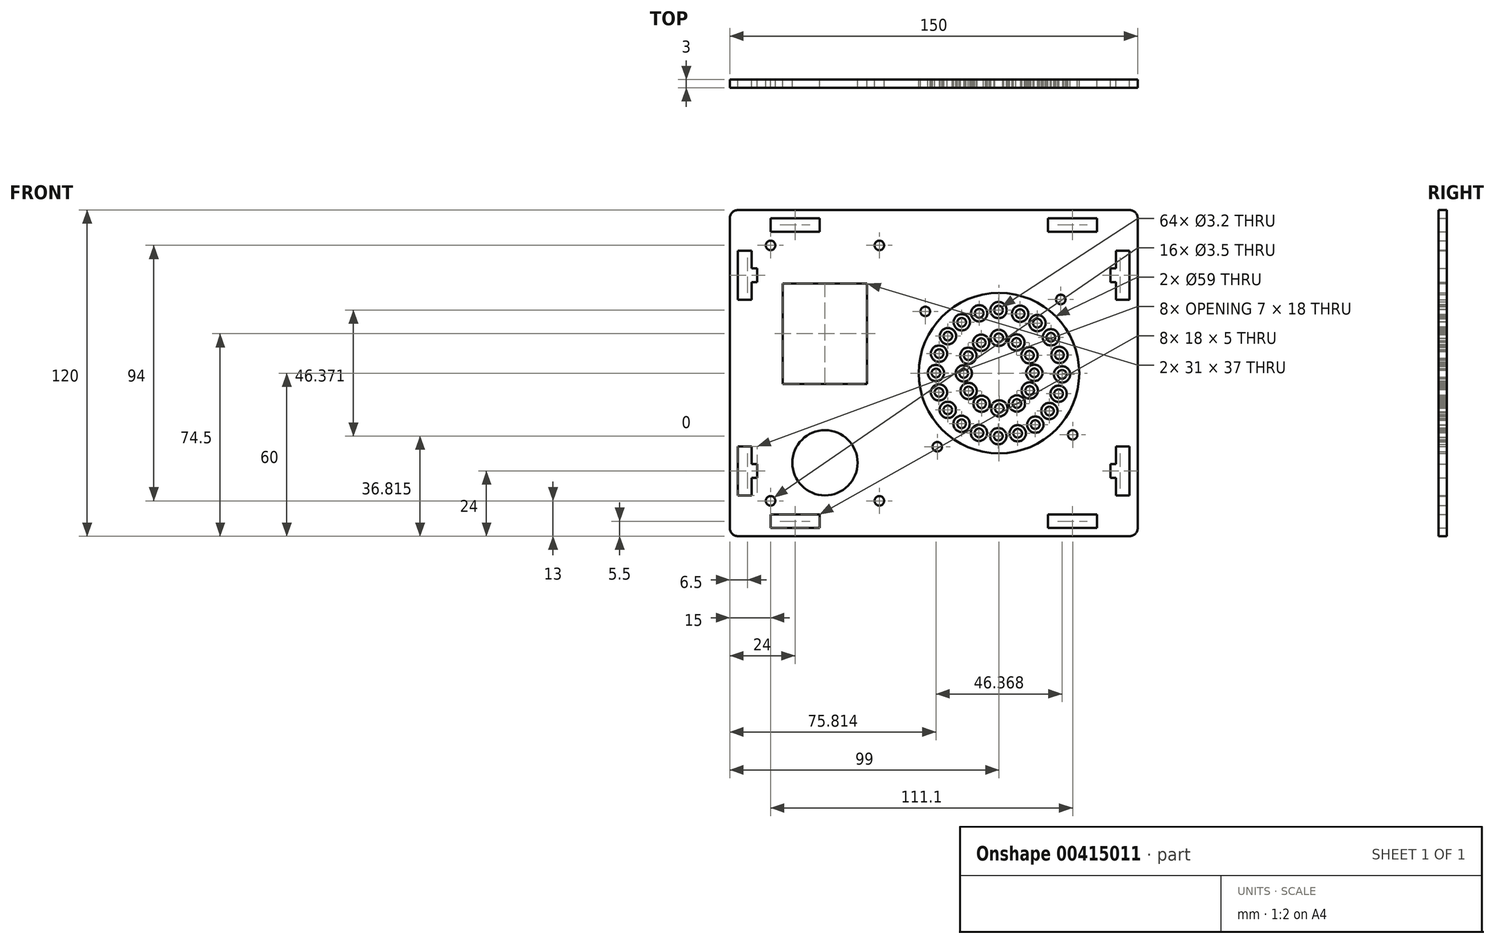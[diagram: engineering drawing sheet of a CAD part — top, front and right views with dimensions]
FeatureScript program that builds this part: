
annotation { "Feature Type Name" : "Feature", "Feature Type Description" : "" }
export const myFeature = defineFeature(function(context is Context, id is Id, definition is map)
    precondition{}
    {
        {
            var Q0;
            Q0=qCreatedBy(makeId("Front.planeOp"),FACE);
            var sketch = newSketch(context, id + "F0", { "sketchPlane" : qUnion([Q0])});
            skLineSegment(sketch, "E0.bottom", {"start": v(-72, 60) * mm, "end": v(72, 60) * mm});
            skLineSegment(sketch, "E0.top", {"start": v(-72, -60) * mm, "end": v(72, -60) * mm});
            skLineSegment(sketch, "E0.left", {"start": v(-75, 57) * mm, "end": v(-75, -57) * mm});
            skLineSegment(sketch, "E0.right", {"start": v(75, 57) * mm, "end": v(75, -57) * mm});
            skPoint(sketch, "E1.visualSharp", {"position": v(-75, 60) * mm});
            skArc(sketch, "E1.filletArc", {"start": v(-72, 60) * mm, "mid": v(-74.12, 59.12) * mm, "end": v(-75, 57) * mm});
            skPoint(sketch, "E2.visualSharp", {"position": v(75, 60) * mm});
            skArc(sketch, "E2.filletArc", {"start": v(75, 57) * mm, "mid": v(74.12, 59.12) * mm, "end": v(72, 60) * mm});
            skPoint(sketch, "E3.visualSharp", {"position": v(75, -60) * mm});
            skArc(sketch, "E3.filletArc", {"start": v(72, -60) * mm, "mid": v(74.12, -59.12) * mm, "end": v(75, -57) * mm});
            skPoint(sketch, "E4.visualSharp", {"position": v(-75, -60) * mm});
            skArc(sketch, "E4.filletArc", {"start": v(-75, -57) * mm, "mid": v(-74.12, -59.12) * mm, "end": v(-72, -60) * mm});
            skLineSegment(sketch, "E5.bottom", {"start": v(-60, 57) * mm, "end": v(-42, 57) * mm});
            skLineSegment(sketch, "E5.top", {"start": v(-60, 52) * mm, "end": v(-42, 52) * mm});
            skLineSegment(sketch, "E5.left", {"start": v(-60, 57) * mm, "end": v(-60, 52) * mm});
            skLineSegment(sketch, "E5.right", {"start": v(-42, 57) * mm, "end": v(-42, 52) * mm});
            skLineSegment(sketch, "E6.bottom", {"start": v(42, 57) * mm, "end": v(60, 57) * mm});
            skLineSegment(sketch, "E6.top", {"start": v(42, 52) * mm, "end": v(60, 52) * mm});
            skLineSegment(sketch, "E6.left", {"start": v(42, 57) * mm, "end": v(42, 52) * mm});
            skLineSegment(sketch, "E6.right", {"start": v(60, 57) * mm, "end": v(60, 52) * mm});
            skLineSegment(sketch, "E7.bottom", {"start": v(72, 45) * mm, "end": v(67, 45) * mm});
            skLineSegment(sketch, "E7.top", {"start": v(72, 27) * mm, "end": v(67, 27) * mm});
            skLineSegment(sketch, "E7.left", {"start": v(72, 45) * mm, "end": v(72, 27) * mm});
            skLineSegment(sketch, "E7.right", {"start": v(67, 45) * mm, "end": v(67, 38.5) * mm});
            skLineSegment(sketch, "E8.bottom", {"start": v(72, -27) * mm, "end": v(67, -27) * mm});
            skLineSegment(sketch, "E8.top", {"start": v(72, -45) * mm, "end": v(67, -45) * mm});
            skLineSegment(sketch, "E8.left", {"start": v(72, -27) * mm, "end": v(72, -45) * mm});
            skLineSegment(sketch, "E8.right", {"start": v(67, -27) * mm, "end": v(67, -33.5) * mm});
            skLineSegment(sketch, "E9.bottom", {"start": v(60, -57) * mm, "end": v(42, -57) * mm});
            skLineSegment(sketch, "E9.top", {"start": v(60, -52) * mm, "end": v(42, -52) * mm});
            skLineSegment(sketch, "E9.left", {"start": v(60, -57) * mm, "end": v(60, -52) * mm});
            skLineSegment(sketch, "E9.right", {"start": v(42, -57) * mm, "end": v(42, -52) * mm});
            skLineSegment(sketch, "E10.bottom", {"start": v(-42, -57) * mm, "end": v(-60, -57) * mm});
            skLineSegment(sketch, "E10.top", {"start": v(-42, -52) * mm, "end": v(-60, -52) * mm});
            skLineSegment(sketch, "E10.left", {"start": v(-42, -57) * mm, "end": v(-42, -52) * mm});
            skLineSegment(sketch, "E10.right", {"start": v(-60, -57) * mm, "end": v(-60, -52) * mm});
            skLineSegment(sketch, "E11.bottom", {"start": v(-67, -27) * mm, "end": v(-72, -27) * mm});
            skLineSegment(sketch, "E11.top", {"start": v(-67, -45) * mm, "end": v(-72, -45) * mm});
            skLineSegment(sketch, "E11.left", {"start": v(-67, -33.5) * mm, "end": v(-67, -27) * mm});
            skLineSegment(sketch, "E11.right", {"start": v(-72, -45) * mm, "end": v(-72, -27) * mm});
            skLineSegment(sketch, "E12.bottom", {"start": v(-67, 27) * mm, "end": v(-72, 27) * mm});
            skLineSegment(sketch, "E12.top", {"start": v(-67, 45) * mm, "end": v(-72, 45) * mm});
            skLineSegment(sketch, "E12.left", {"start": v(-67, 27) * mm, "end": v(-67, 33.5) * mm});
            skLineSegment(sketch, "E12.right", {"start": v(-72, 27) * mm, "end": v(-72, 45) * mm});
            skCircle(sketch, "E13", {"center": v(24, 0) * mm, "radius": 29.5 * mm});
            skCircle(sketch, "E14", {"center": v(46.7, 27.1) * mm, "radius": 1.75 * mm});
            skCircle(sketch, "E15", {"center": v(-3.1, 22.7) * mm, "radius": 1.75 * mm});
            skCircle(sketch, "E16", {"center": v(1.3, -27.1) * mm, "radius": 1.75 * mm});
            skCircle(sketch, "E17", {"center": v(51.1, -22.7) * mm, "radius": 1.75 * mm});
            skLineSegment(sketch, "E18", {"start": v(-75, 0) * mm, "end": v(75, 0) * mm, "construction": true});
            skLineSegment(sketch, "E19.bottom", {"start": v(-17, 50) * mm, "end": v(-63, 50) * mm, "construction": true});
            skLineSegment(sketch, "E19.top", {"start": v(-17, -50) * mm, "end": v(-63, -50) * mm, "construction": true});
            skLineSegment(sketch, "E19.left", {"start": v(-17, 50) * mm, "end": v(-17, -50) * mm, "construction": true});
            skLineSegment(sketch, "E19.right", {"start": v(-63, 50) * mm, "end": v(-63, -50) * mm, "construction": true});
            skPoint(sketch, "E19.middle", {"position": v(-40, 0) * mm});
            skLineSegment(sketch, "E20", {"start": v(-40, 0) * mm, "end": v(-40, 15.63) * mm, "construction": true});
            skCircle(sketch, "E21", {"center": v(-60, 47) * mm, "radius": 1.75 * mm});
            skCircle(sketch, "E22.MirrorC", {"center": v(-20, 47) * mm, "radius": 1.75 * mm});
            skCircle(sketch, "E23.MirrorC", {"center": v(-20, -47) * mm, "radius": 1.75 * mm});
            skCircle(sketch, "E24.MirrorC", {"center": v(-60, -47) * mm, "radius": 1.75 * mm});
            skLineSegment(sketch, "E25.bottom", {"start": v(-24.5, -4) * mm, "end": v(-55.5, -4) * mm});
            skLineSegment(sketch, "E25.top", {"start": v(-24.5, 33) * mm, "end": v(-55.5, 33) * mm});
            skLineSegment(sketch, "E25.left", {"start": v(-24.5, -4) * mm, "end": v(-24.5, 33) * mm});
            skLineSegment(sketch, "E25.right", {"start": v(-55.5, -4) * mm, "end": v(-55.5, 33) * mm});
            skPoint(sketch, "E25.middle", {"position": v(-40, 14.5) * mm});
            skCircle(sketch, "E26", {"center": v(-40, -33) * mm, "radius": 12 * mm});
            skLineSegment(sketch, "E27.bottom", {"start": v(62, -43) * mm, "end": v(-14, -43) * mm, "construction": true});
            skLineSegment(sketch, "E27.top", {"start": v(62, 43) * mm, "end": v(-14, 43) * mm, "construction": true});
            skLineSegment(sketch, "E27.left", {"start": v(62, -43) * mm, "end": v(62, 43) * mm, "construction": true});
            skLineSegment(sketch, "E27.right", {"start": v(-14, -43) * mm, "end": v(-14, 43) * mm, "construction": true});
            skLineSegment(sketch, "E28", {"start": v(-67, 38.5) * mm, "end": v(-65, 38.5) * mm});
            skLineSegment(sketch, "E29", {"start": v(-65, 38.5) * mm, "end": v(-65, 33.5) * mm});
            skLineSegment(sketch, "E30", {"start": v(-65, 33.5) * mm, "end": v(-67, 33.5) * mm});
            skLineSegment(sketch, "E31.trimOffspring", {"start": v(-67, 38.5) * mm, "end": v(-67, 45) * mm});
            skLineSegment(sketch, "E32", {"start": v(-72, 36) * mm, "end": v(-68.51, 36) * mm, "construction": true});
            skPoint(sketch, "E32.endSnap0", {"position": v(-72, 36) * mm});
            skLineSegment(sketch, "E33.MirrorCS", {"start": v(65, 38.5) * mm, "end": v(65, 33.5) * mm});
            skLineSegment(sketch, "E34.MirrorCS", {"start": v(67, 38.5) * mm, "end": v(65, 38.5) * mm});
            skLineSegment(sketch, "E35.MirrorCS", {"start": v(65, 33.5) * mm, "end": v(67, 33.5) * mm});
            skLineSegment(sketch, "E36.MirrorCS", {"start": v(-67, -38.5) * mm, "end": v(-65, -38.5) * mm});
            skLineSegment(sketch, "E37.MirrorCS", {"start": v(-65, -38.5) * mm, "end": v(-65, -33.5) * mm});
            skLineSegment(sketch, "E38.MirrorCS", {"start": v(-65, -33.5) * mm, "end": v(-67, -33.5) * mm});
            skLineSegment(sketch, "E39.MirrorCS", {"start": v(67, -38.5) * mm, "end": v(65, -38.5) * mm});
            skLineSegment(sketch, "E40.MirrorCS", {"start": v(65, -38.5) * mm, "end": v(65, -33.5) * mm});
            skLineSegment(sketch, "E41.MirrorCS", {"start": v(65, -33.5) * mm, "end": v(67, -33.5) * mm});
            skLineSegment(sketch, "E42.trimOffspring", {"start": v(67, 33.5) * mm, "end": v(67, 27) * mm});
            skLineSegment(sketch, "E43.trimOffspring", {"start": v(67, -38.5) * mm, "end": v(67, -45) * mm});
            skLineSegment(sketch, "E44.trimOffspring", {"start": v(-67, -45) * mm, "end": v(-67, -38.5) * mm});
            skSolve(sketch);
        }
        {
            var Q0;
            Q0=makeQuery(id+"F0.imprint","IMPRINT",FACE,{"disambiguationData":[TD([[makeQuery(id+"F0.imprint","IMPRINT",EDGE,{"derivedFrom":sQuery(id+"F0.wireOp",EDGE,"E0.bottom")}),-1.0]])]});
            extrude(context, id + "F1", {"entities" : qUnion([Q0]), "depth" : 3 * mm});
        }
        {
            var Q0;
            Q0=makeQuery(id+"F1.opExtrude","CAP_FACE",FACE,{"disambiguationData":[OSD([sQuery(id+"F0.wireOp",EDGE,"E0.bottom"),sQuery(id+"F0.wireOp",EDGE,"E0.top"),sQuery(id+"F0.wireOp",EDGE,"E0.left"),sQuery(id+"F0.wireOp",EDGE,"E0.right"),sQuery(id+"F0.wireOp",EDGE,"E1.filletArc"),sQuery(id+"F0.wireOp",EDGE,"E2.filletArc"),sQuery(id+"F0.wireOp",EDGE,"E3.filletArc"),sQuery(id+"F0.wireOp",EDGE,"E4.filletArc"),sQuery(id+"F0.wireOp",EDGE,"E5.bottom"),sQuery(id+"F0.wireOp",EDGE,"E5.top"),sQuery(id+"F0.wireOp",EDGE,"E5.left"),sQuery(id+"F0.wireOp",EDGE,"E5.right"),sQuery(id+"F0.wireOp",EDGE,"E6.bottom"),sQuery(id+"F0.wireOp",EDGE,"E6.top"),sQuery(id+"F0.wireOp",EDGE,"E6.left"),sQuery(id+"F0.wireOp",EDGE,"E6.right"),sQuery(id+"F0.wireOp",EDGE,"E7.bottom"),sQuery(id+"F0.wireOp",EDGE,"E7.top"),sQuery(id+"F0.wireOp",EDGE,"E7.left"),sQuery(id+"F0.wireOp",EDGE,"E7.right"),sQuery(id+"F0.wireOp",EDGE,"E8.bottom"),sQuery(id+"F0.wireOp",EDGE,"E8.top"),sQuery(id+"F0.wireOp",EDGE,"E8.left"),sQuery(id+"F0.wireOp",EDGE,"E8.right"),sQuery(id+"F0.wireOp",EDGE,"E9.bottom"),sQuery(id+"F0.wireOp",EDGE,"E9.top"),sQuery(id+"F0.wireOp",EDGE,"E9.left"),sQuery(id+"F0.wireOp",EDGE,"E9.right"),sQuery(id+"F0.wireOp",EDGE,"E10.bottom"),sQuery(id+"F0.wireOp",EDGE,"E10.top"),sQuery(id+"F0.wireOp",EDGE,"E10.left"),sQuery(id+"F0.wireOp",EDGE,"E10.right"),sQuery(id+"F0.wireOp",EDGE,"E11.bottom"),sQuery(id+"F0.wireOp",EDGE,"E11.top"),sQuery(id+"F0.wireOp",EDGE,"E11.left"),sQuery(id+"F0.wireOp",EDGE,"E11.right"),sQuery(id+"F0.wireOp",EDGE,"E12.bottom"),sQuery(id+"F0.wireOp",EDGE,"E12.top"),sQuery(id+"F0.wireOp",EDGE,"E12.left"),sQuery(id+"F0.wireOp",EDGE,"E12.right"),sQuery(id+"F0.wireOp",EDGE,"E13"),sQuery(id+"F0.wireOp",EDGE,"E14"),sQuery(id+"F0.wireOp",EDGE,"E15"),sQuery(id+"F0.wireOp",EDGE,"E16"),sQuery(id+"F0.wireOp",EDGE,"E17"),sQuery(id+"F0.wireOp",EDGE,"E21"),sQuery(id+"F0.wireOp",EDGE,"E22.MirrorC"),sQuery(id+"F0.wireOp",EDGE,"E23.MirrorC"),sQuery(id+"F0.wireOp",EDGE,"E24.MirrorC"),sQuery(id+"F0.wireOp",EDGE,"E25.bottom"),sQuery(id+"F0.wireOp",EDGE,"E25.top"),sQuery(id+"F0.wireOp",EDGE,"E25.left"),sQuery(id+"F0.wireOp",EDGE,"E25.right"),sQuery(id+"F0.wireOp",EDGE,"E26"),sQuery(id+"F0.wireOp",EDGE,"E28"),sQuery(id+"F0.wireOp",EDGE,"E29"),sQuery(id+"F0.wireOp",EDGE,"E30"),sQuery(id+"F0.wireOp",EDGE,"E31.trimOffspring"),sQuery(id+"F0.wireOp",EDGE,"E33.MirrorCS"),sQuery(id+"F0.wireOp",EDGE,"E34.MirrorCS"),sQuery(id+"F0.wireOp",EDGE,"E35.MirrorCS"),sQuery(id+"F0.wireOp",EDGE,"E36.MirrorCS"),sQuery(id+"F0.wireOp",EDGE,"E37.MirrorCS"),sQuery(id+"F0.wireOp",EDGE,"E38.MirrorCS"),sQuery(id+"F0.wireOp",EDGE,"E39.MirrorCS"),sQuery(id+"F0.wireOp",EDGE,"E40.MirrorCS"),sQuery(id+"F0.wireOp",EDGE,"E41.MirrorCS"),sQuery(id+"F0.wireOp",EDGE,"E42.trimOffspring"),sQuery(id+"F0.wireOp",EDGE,"E43.trimOffspring"),sQuery(id+"F0.wireOp",EDGE,"E44.trimOffspring")])],"isStart":true});
            var sketch = newSketch(context, id + "F2", { "sketchPlane" : qUnion([Q0])});
            skCircle(sketch, "E45", {"center": v(-23.83, 23.19) * mm, "radius": 3 * mm});
            skCircle(sketch, "E46", {"center": v(-23.83, 23.19) * mm, "radius": 1.6 * mm});
            skCircle(sketch, "E47.1.0", {"center": v(-16.71, 22.01) * mm, "radius": 1.6 * mm});
            skCircle(sketch, "E47.1.1", {"center": v(-16.71, 22.01) * mm, "radius": 3 * mm});
            skCircle(sketch, "E47.2.0", {"center": v(-10.3, 18.7) * mm, "radius": 1.6 * mm});
            skCircle(sketch, "E47.2.1", {"center": v(-10.3, 18.7) * mm, "radius": 3 * mm});
            skCircle(sketch, "E47.3.0", {"center": v(-5.22, 13.6) * mm, "radius": 1.6 * mm});
            skCircle(sketch, "E47.3.1", {"center": v(-5.22, 13.6) * mm, "radius": 3 * mm});
            skCircle(sketch, "E47.4.0", {"center": v(-1.95, 7.17) * mm, "radius": 1.6 * mm});
            skCircle(sketch, "E47.4.1", {"center": v(-1.95, 7.17) * mm, "radius": 3 * mm});
            skCircle(sketch, "E47.5.0", {"center": v(-0.81, 0.04) * mm, "radius": 1.6 * mm});
            skCircle(sketch, "E47.5.1", {"center": v(-0.81, 0.04) * mm, "radius": 3 * mm});
            skCircle(sketch, "E47.6.0", {"center": v(-1.92, -7.08) * mm, "radius": 1.6 * mm});
            skCircle(sketch, "E47.6.1", {"center": v(-1.92, -7.08) * mm, "radius": 3 * mm});
            skCircle(sketch, "E47.7.0", {"center": v(-5.17, -13.52) * mm, "radius": 1.6 * mm});
            skCircle(sketch, "E47.7.1", {"center": v(-5.17, -13.52) * mm, "radius": 3 * mm});
            skCircle(sketch, "E47.8.0", {"center": v(-10.23, -18.66) * mm, "radius": 1.6 * mm});
            skCircle(sketch, "E47.8.1", {"center": v(-10.23, -18.66) * mm, "radius": 3 * mm});
            skCircle(sketch, "E47.9.0", {"center": v(-16.63, -21.98) * mm, "radius": 1.6 * mm});
            skCircle(sketch, "E47.9.1", {"center": v(-16.63, -21.98) * mm, "radius": 3 * mm});
            skCircle(sketch, "E47.10.0", {"center": v(-23.74, -23.19) * mm, "radius": 1.6 * mm});
            skCircle(sketch, "E47.10.1", {"center": v(-23.74, -23.19) * mm, "radius": 3 * mm});
            skCircle(sketch, "E47.11.0", {"center": v(-30.88, -22.14) * mm, "radius": 1.6 * mm});
            skCircle(sketch, "E47.11.1", {"center": v(-30.88, -22.14) * mm, "radius": 3 * mm});
            skCircle(sketch, "E47.12.0", {"center": v(-37.35, -18.96) * mm, "radius": 1.6 * mm});
            skCircle(sketch, "E47.12.1", {"center": v(-37.35, -18.96) * mm, "radius": 3 * mm});
            skCircle(sketch, "E47.13.0", {"center": v(-42.53, -13.94) * mm, "radius": 1.6 * mm});
            skCircle(sketch, "E47.13.1", {"center": v(-42.53, -13.94) * mm, "radius": 3 * mm});
            skCircle(sketch, "E47.14.0", {"center": v(-45.92, -7.57) * mm, "radius": 1.6 * mm});
            skCircle(sketch, "E47.14.1", {"center": v(-45.92, -7.57) * mm, "radius": 3 * mm});
            skCircle(sketch, "E47.15.0", {"center": v(-47.18, -0.47) * mm, "radius": 1.6 * mm});
            skCircle(sketch, "E47.15.1", {"center": v(-47.18, -0.47) * mm, "radius": 3 * mm});
            skCircle(sketch, "E47.16.0", {"center": v(-46.2, 6.68) * mm, "radius": 1.6 * mm});
            skCircle(sketch, "E47.16.1", {"center": v(-46.2, 6.68) * mm, "radius": 3 * mm});
            skCircle(sketch, "E47.17.0", {"center": v(-43.08, 13.18) * mm, "radius": 1.6 * mm});
            skCircle(sketch, "E47.17.1", {"center": v(-43.08, 13.18) * mm, "radius": 3 * mm});
            skCircle(sketch, "E47.18.0", {"center": v(-38.1, 18.4) * mm, "radius": 1.6 * mm});
            skCircle(sketch, "E47.18.1", {"center": v(-38.1, 18.4) * mm, "radius": 3 * mm});
            skCircle(sketch, "E47.19.0", {"center": v(-31.77, 21.85) * mm, "radius": 1.6 * mm});
            skCircle(sketch, "E47.19.1", {"center": v(-31.77, 21.85) * mm, "radius": 3 * mm});
            skPoint(sketch, "E47.center", {"position": v(-24, 0) * mm});
            skLineSegment(sketch, "E47.anchor1", {"start": v(-24, 0) * mm, "end": v(-23.83, 23.19) * mm, "construction": true});
            skLineSegment(sketch, "E47.anchor2", {"start": v(-24, 0) * mm, "end": v(-31.77, 21.85) * mm, "construction": true});
            skCircle(sketch, "E48", {"center": v(-23.9, 12.97) * mm, "radius": 3 * mm});
            skCircle(sketch, "E49", {"center": v(-23.9, 12.97) * mm, "radius": 1.6 * mm});
            skCircle(sketch, "E50.1.0", {"center": v(-17.43, 11.19) * mm, "radius": 3 * mm});
            skCircle(sketch, "E50.1.1", {"center": v(-17.43, 11.19) * mm, "radius": 1.6 * mm});
            skCircle(sketch, "E50.2.0", {"center": v(-12.72, 6.4) * mm, "radius": 3 * mm});
            skCircle(sketch, "E50.2.1", {"center": v(-12.72, 6.4) * mm, "radius": 1.6 * mm});
            skCircle(sketch, "E50.3.0", {"center": v(-11.03, -0.1) * mm, "radius": 3 * mm});
            skCircle(sketch, "E50.3.1", {"center": v(-11.03, -0.1) * mm, "radius": 1.6 * mm});
            skCircle(sketch, "E50.4.0", {"center": v(-12.81, -6.57) * mm, "radius": 3 * mm});
            skCircle(sketch, "E50.4.1", {"center": v(-12.81, -6.57) * mm, "radius": 1.6 * mm});
            skCircle(sketch, "E50.5.0", {"center": v(-17.6, -11.28) * mm, "radius": 3 * mm});
            skCircle(sketch, "E50.5.1", {"center": v(-17.6, -11.28) * mm, "radius": 1.6 * mm});
            skCircle(sketch, "E50.6.0", {"center": v(-24.1, -12.97) * mm, "radius": 3 * mm});
            skCircle(sketch, "E50.6.1", {"center": v(-24.1, -12.97) * mm, "radius": 1.6 * mm});
            skCircle(sketch, "E50.7.0", {"center": v(-30.57, -11.19) * mm, "radius": 3 * mm});
            skCircle(sketch, "E50.7.1", {"center": v(-30.57, -11.19) * mm, "radius": 1.6 * mm});
            skCircle(sketch, "E50.8.0", {"center": v(-35.28, -6.4) * mm, "radius": 3 * mm});
            skCircle(sketch, "E50.8.1", {"center": v(-35.28, -6.4) * mm, "radius": 1.6 * mm});
            skCircle(sketch, "E50.9.0", {"center": v(-36.97, 0.1) * mm, "radius": 3 * mm});
            skCircle(sketch, "E50.9.1", {"center": v(-36.97, 0.1) * mm, "radius": 1.6 * mm});
            skCircle(sketch, "E50.10.0", {"center": v(-35.19, 6.57) * mm, "radius": 3 * mm});
            skCircle(sketch, "E50.10.1", {"center": v(-35.19, 6.57) * mm, "radius": 1.6 * mm});
            skCircle(sketch, "E50.11.0", {"center": v(-30.4, 11.28) * mm, "radius": 3 * mm});
            skCircle(sketch, "E50.11.1", {"center": v(-30.4, 11.28) * mm, "radius": 1.6 * mm});
            skLineSegment(sketch, "E50.anchor1", {"start": v(-24, 0) * mm, "end": v(-23.9, 12.97) * mm, "construction": true});
            skLineSegment(sketch, "E50.anchor2", {"start": v(-24, 0) * mm, "end": v(-30.4, 11.28) * mm, "construction": true});
            skSolve(sketch);
        }
        {
            var Q0;
            Q0 = qSketchRegion(id + "F2", true);
            extrude(context, id + "F3", {"entities" : qUnion([Q0]), "oppositeDirection" : true, "depth" : 3 * mm});
        }
    });
